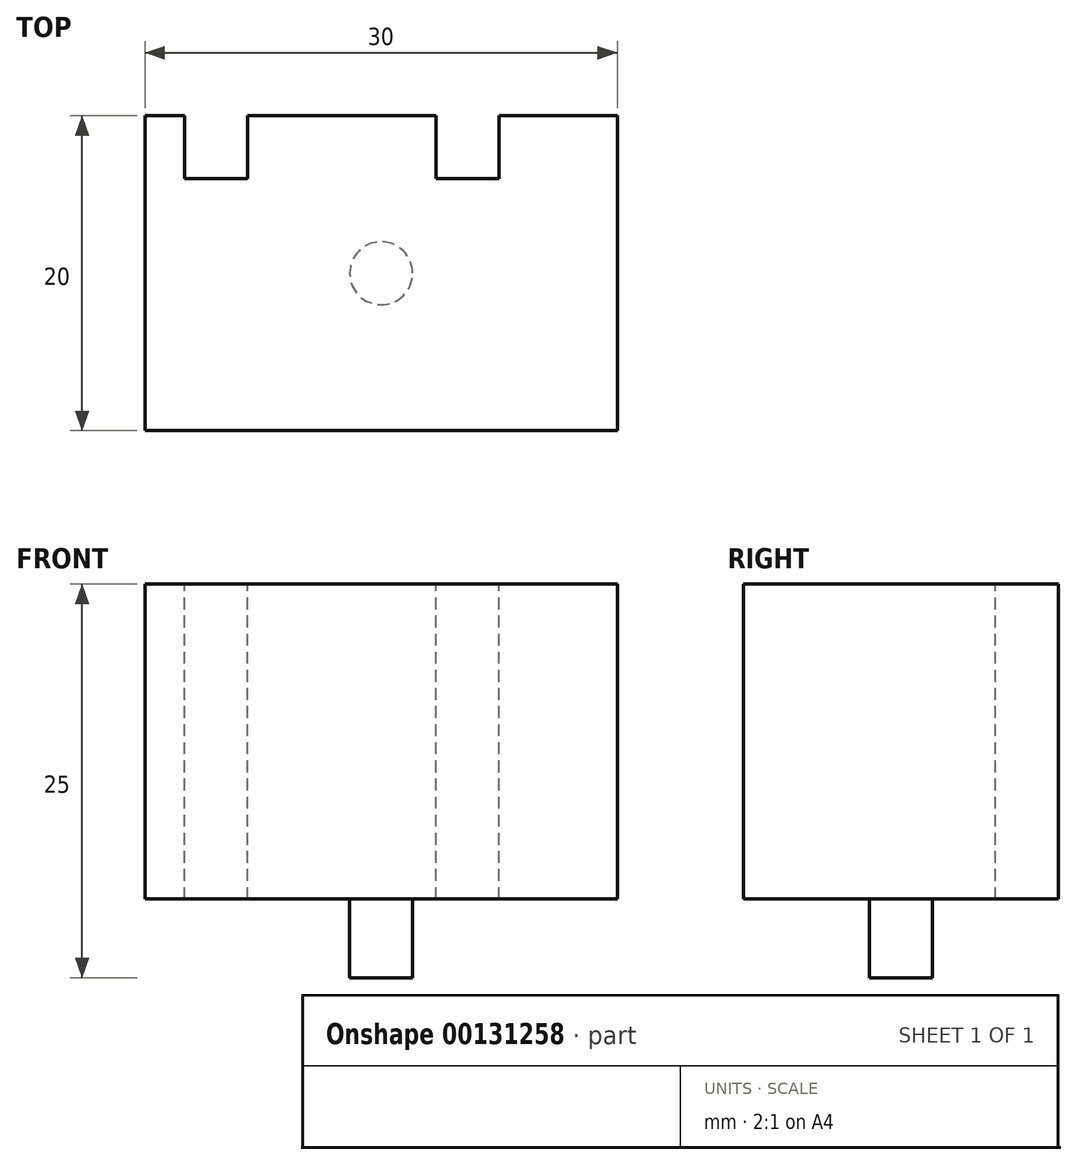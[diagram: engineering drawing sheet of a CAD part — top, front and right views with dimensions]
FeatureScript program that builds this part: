
annotation { "Feature Type Name" : "Feature", "Feature Type Description" : "" }
export const myFeature = defineFeature(function(context is Context, id is Id, definition is map)
    precondition{}
    {
        {
            var Q0;
            Q0=qCreatedBy(makeId("Top.planeOp"),FACE);
            var sketch = newSketch(context, id + "F0", { "sketchPlane" : qUnion([Q0])});
            skLineSegment(sketch, "E0", {"start": v(0, 0) * mm, "end": v(30, 0) * mm});
            skLineSegment(sketch, "E1", {"start": v(30, 0) * mm, "end": v(30, 20) * mm});
            skLineSegment(sketch, "E2", {"start": v(30, 20) * mm, "end": v(0, 20) * mm});
            skLineSegment(sketch, "E3", {"start": v(0, 20) * mm, "end": v(0, 0) * mm});
            skSolve(sketch);
        }
        {
            var Q0;
            Q0=makeQuery(id+"F0.imprint","IMPRINT",FACE,{"disambiguationData":[TD([[makeQuery(id+"F0.imprint","IMPRINT",EDGE,{"derivedFrom":sQuery(id+"F0.wireOp",EDGE,"E0")}),1.0]])]});
            extrude(context, id + "F1", {"entities" : qUnion([Q0]), "depth" : 20 * mm});
        }
        {
            var Q0;
            Q0=makeQuery(id+"F1.opExtrude","CAP_FACE",FACE,{"disambiguationData":[OSD([sQuery(id+"F0.wireOp",EDGE,"E0"),sQuery(id+"F0.wireOp",EDGE,"E1"),sQuery(id+"F0.wireOp",EDGE,"E2"),sQuery(id+"F0.wireOp",EDGE,"E3")])],"isStart":false});
            var sketch = newSketch(context, id + "F2", { "sketchPlane" : qUnion([Q0])});
            skLineSegment(sketch, "E4", {"start": v(22.5, 20) * mm, "end": v(22.5, 16) * mm});
            skLineSegment(sketch, "E5", {"start": v(22.5, 16) * mm, "end": v(18.5, 16) * mm});
            skLineSegment(sketch, "E6", {"start": v(18.5, 16) * mm, "end": v(18.5, 20) * mm});
            skLineSegment(sketch, "E7", {"start": v(18.5, 20) * mm, "end": v(22.5, 20) * mm});
            skLineSegment(sketch, "E8", {"start": v(2.5, 20) * mm, "end": v(2.5, 16) * mm});
            skLineSegment(sketch, "E9", {"start": v(2.5, 16) * mm, "end": v(6.5, 16) * mm});
            skLineSegment(sketch, "E10", {"start": v(6.5, 16) * mm, "end": v(6.5, 20) * mm});
            skLineSegment(sketch, "E11", {"start": v(6.5, 20) * mm, "end": v(2.5, 20) * mm});
            skSolve(sketch);
        }
        {
            var Q0;
            Q0=makeQuery(id+"F2.imprint","IMPRINT",FACE,{"disambiguationData":[TD([[makeQuery(id+"F2.imprint","IMPRINT",EDGE,{"derivedFrom":sQuery(id+"F2.wireOp",EDGE,"E8")}),1.0]])]});
            var Q1;
            Q1=makeQuery(id+"F2.imprint","IMPRINT",FACE,{"disambiguationData":[TD([[makeQuery(id+"F2.imprint","IMPRINT",EDGE,{"derivedFrom":sQuery(id+"F2.wireOp",EDGE,"E4")}),-1.0]])]});
            extrude(context, id + "F3", {"entities" : qUnion([Q0, Q1]), "operationType" : NewBodyOperationType.REMOVE, "endBound" : BoundingType.THROUGH_ALL, "oppositeDirection" : true, "depth" : 25 * mm});
        }
        {
            var Q0;
            Q0=makeQuery(id+"F1.opExtrude","CAP_FACE",FACE,{"disambiguationData":[OSD([sQuery(id+"F0.wireOp",EDGE,"E0"),sQuery(id+"F0.wireOp",EDGE,"E1"),sQuery(id+"F0.wireOp",EDGE,"E2"),sQuery(id+"F0.wireOp",EDGE,"E3")])],"isStart":true});
            var sketch = newSketch(context, id + "F4", { "sketchPlane" : qUnion([Q0])});
            skLineSegment(sketch, "E12", {"start": v(0, -10) * mm, "end": v(30, -10) * mm});
            skLineSegment(sketch, "E13", {"start": v(15, 0) * mm, "end": v(15, -20) * mm});
            skPoint(sketch, "E13.endSnap0", {"position": v(12.5, -20) * mm});
            skCircle(sketch, "E14", {"center": v(15, -10) * mm, "radius": 2 * mm});
            skSolve(sketch);
        }
        {
            var Q0;
            Q0 = qSketchRegion(id + "F4", true);
            extrude(context, id + "F5", {"entities" : qUnion([Q0]), "operationType" : NewBodyOperationType.ADD, "depth" : 5 * mm});
        }
    });
